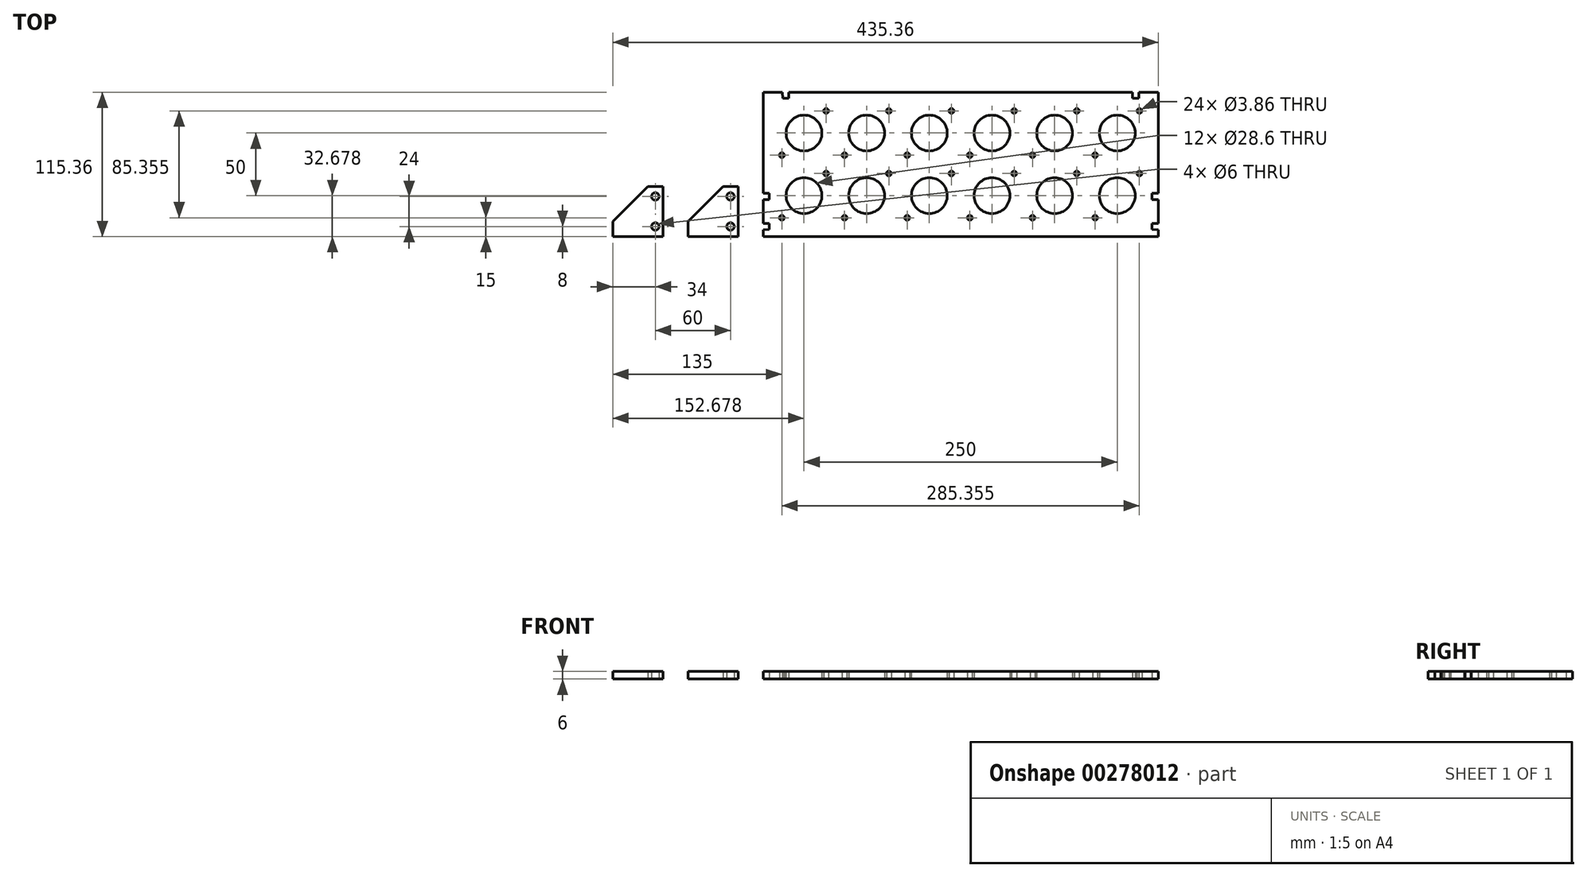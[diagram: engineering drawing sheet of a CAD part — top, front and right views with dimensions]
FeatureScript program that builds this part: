
annotation { "Feature Type Name" : "Feature", "Feature Type Description" : "" }
export const myFeature = defineFeature(function(context is Context, id is Id, definition is map)
    precondition{}
    {
        {
            assignVariable(context, id + "F0", {"name" : "X", "anyValue" : 6 * mm});
        }
        {
            var Q0;
            Q0=qCreatedBy(makeId("Top.planeOp"),FACE);
            var sketch = newSketch(context, id + "F1", { "sketchPlane" : qUnion([Q0])});
            skCircle(sketch, "E0", {"center": v(32.68, 32.68) * mm, "radius": 13.5 * mm, "construction": true});
            skCircle(sketch, "E1", {"center": v(15, 15) * mm, "radius": 1.93 * mm});
            skCircle(sketch, "E2", {"center": v(32.68, 32.68) * mm, "radius": 14.3 * mm});
            skCircle(sketch, "E3", {"center": v(50.36, 50.36) * mm, "radius": 1.93 * mm});
            skLineSegment(sketch, "E4", {"start": v(15, 15) * mm, "end": v(50.36, 50.36) * mm, "construction": true});
            skCircle(sketch, "E5.0.1.0", {"center": v(50.36, 100.36) * mm, "radius": 1.93 * mm});
            skCircle(sketch, "E5.0.1.1", {"center": v(32.68, 82.68) * mm, "radius": 14.3 * mm});
            skCircle(sketch, "E5.0.1.2", {"center": v(15, 65) * mm, "radius": 1.93 * mm});
            skCircle(sketch, "E5.1.0.0", {"center": v(100.36, 50.36) * mm, "radius": 1.93 * mm});
            skCircle(sketch, "E5.1.0.1", {"center": v(82.68, 32.68) * mm, "radius": 14.3 * mm});
            skCircle(sketch, "E5.1.0.2", {"center": v(65, 15) * mm, "radius": 1.93 * mm});
            skCircle(sketch, "E5.1.1.0", {"center": v(100.36, 100.36) * mm, "radius": 1.93 * mm});
            skCircle(sketch, "E5.1.1.1", {"center": v(82.68, 82.68) * mm, "radius": 14.3 * mm});
            skCircle(sketch, "E5.1.1.2", {"center": v(65, 65) * mm, "radius": 1.93 * mm});
            skCircle(sketch, "E5.2.0.0", {"center": v(150.36, 50.36) * mm, "radius": 1.93 * mm});
            skCircle(sketch, "E5.2.0.1", {"center": v(132.68, 32.68) * mm, "radius": 14.3 * mm});
            skCircle(sketch, "E5.2.0.2", {"center": v(115, 15) * mm, "radius": 1.93 * mm});
            skCircle(sketch, "E5.2.1.0", {"center": v(150.36, 100.36) * mm, "radius": 1.93 * mm});
            skCircle(sketch, "E5.2.1.1", {"center": v(132.68, 82.68) * mm, "radius": 14.3 * mm});
            skCircle(sketch, "E5.2.1.2", {"center": v(115, 65) * mm, "radius": 1.93 * mm});
            skCircle(sketch, "E5.3.0.0", {"center": v(200.36, 50.36) * mm, "radius": 1.93 * mm});
            skCircle(sketch, "E5.3.0.1", {"center": v(182.68, 32.68) * mm, "radius": 14.3 * mm});
            skCircle(sketch, "E5.3.0.2", {"center": v(165, 15) * mm, "radius": 1.93 * mm});
            skCircle(sketch, "E5.3.1.0", {"center": v(200.36, 100.36) * mm, "radius": 1.93 * mm});
            skCircle(sketch, "E5.3.1.1", {"center": v(182.68, 82.68) * mm, "radius": 14.3 * mm});
            skCircle(sketch, "E5.3.1.2", {"center": v(165, 65) * mm, "radius": 1.93 * mm});
            skLineSegment(sketch, "E5.direction1", {"start": v(15, 15) * mm, "end": v(65, 15) * mm, "construction": true});
            skLineSegment(sketch, "E5.direction2", {"start": v(15, 15) * mm, "end": v(15, 65) * mm, "construction": true});
            skCircle(sketch, "E6.0.4.0", {"center": v(250.36, 50.36) * mm, "radius": 1.93 * mm});
            skCircle(sketch, "E6.2.4.0", {"center": v(232.68, 32.68) * mm, "radius": 14.3 * mm});
            skCircle(sketch, "E6.4.4.0", {"center": v(215, 15) * mm, "radius": 1.93 * mm});
            skCircle(sketch, "E6.0.4.1", {"center": v(250.36, 100.36) * mm, "radius": 1.93 * mm});
            skCircle(sketch, "E6.2.4.1", {"center": v(232.68, 82.68) * mm, "radius": 14.3 * mm});
            skCircle(sketch, "E6.4.4.1", {"center": v(215, 65) * mm, "radius": 1.93 * mm});
            skCircle(sketch, "E6.0.5.0", {"center": v(300.36, 50.36) * mm, "radius": 1.93 * mm});
            skCircle(sketch, "E6.2.5.0", {"center": v(282.68, 32.68) * mm, "radius": 14.3 * mm});
            skCircle(sketch, "E6.4.5.0", {"center": v(265, 15) * mm, "radius": 1.93 * mm});
            skCircle(sketch, "E6.0.5.1", {"center": v(300.36, 100.36) * mm, "radius": 1.93 * mm});
            skCircle(sketch, "E6.2.5.1", {"center": v(282.68, 82.68) * mm, "radius": 14.3 * mm});
            skCircle(sketch, "E6.4.5.1", {"center": v(265, 65) * mm, "radius": 1.93 * mm});
            skLineSegment(sketch, "E7.bottom", {"start": v(0, 0) * mm, "end": v(315.36, 0) * mm});
            skLineSegment(sketch, "E7.top", {"start": v(0, 115.36) * mm, "end": v(15.4, 115.36) * mm});
            skLineSegment(sketch, "E8", {"start": v(300.36, 100.36) * mm, "end": v(300.36, 115.36) * mm, "construction": true});
            skLineSegment(sketch, "E9", {"start": v(300.36, 100.36) * mm, "end": v(315.36, 100.36) * mm, "construction": true});
            skLineSegment(sketch, "E10", {"start": v(15, 15) * mm, "end": v(0, 15) * mm, "construction": true});
            skLineSegment(sketch, "E11", {"start": v(15, 15) * mm, "end": v(15, 0) * mm, "construction": true});
            skLineSegment(sketch, "E12", {"start": v(-32, 40) * mm, "end": v(-60, 12) * mm});
            skLineSegment(sketch, "E13", {"start": v(-60, 12) * mm, "end": v(-60, 0) * mm});
            skLineSegment(sketch, "E14", {"start": v(-60, 0) * mm, "end": v(-20, 0) * mm});
            skLineSegment(sketch, "E15.trimOffspring", {"start": v(0, 0) * mm, "end": v(0, 5.4) * mm});
            skLineSegment(sketch, "E16.trimOffspring", {"start": v(315.36, 0) * mm, "end": v(315.36, 5.4) * mm});
            skLineSegment(sketch, "E17", {"start": v(-20, 0) * mm, "end": v(-20, 40) * mm});
            skLineSegment(sketch, "E18", {"start": v(-20, 40) * mm, "end": v(-23, 40) * mm});
            skLineSegment(sketch, "E19", {"start": v(-23, 40) * mm, "end": v(-23, 0) * mm, "construction": true});
            skLineSegment(sketch, "E20", {"start": v(-26, 0) * mm, "end": v(-26, 40) * mm, "construction": true});
            skLineSegment(sketch, "E21", {"start": v(-29, 40) * mm, "end": v(-29, 0) * mm, "construction": true});
            skLineSegment(sketch, "E22", {"start": v(-29, 40) * mm, "end": v(-32, 40) * mm});
            skLineSegment(sketch, "E23", {"start": v(-26, 40) * mm, "end": v(-29, 40) * mm});
            skLineSegment(sketch, "E24", {"start": v(-23, 40) * mm, "end": v(-26, 40) * mm});
            skCircle(sketch, "E25", {"center": v(-26, 32) * mm, "radius": 3 * mm});
            skCircle(sketch, "E26", {"center": v(-26, 8) * mm, "radius": 3 * mm});
            skLineSegment(sketch, "E27", {"start": v(0, 34.6) * mm, "end": v(5, 34.45) * mm});
            skLineSegment(sketch, "E28", {"start": v(5, 34.45) * mm, "end": v(5, 29.55) * mm});
            skLineSegment(sketch, "E29", {"start": v(5, 29.55) * mm, "end": v(0, 29.4) * mm});
            skLineSegment(sketch, "E30.trimOffspring", {"start": v(0, 34.6) * mm, "end": v(0, 115.36) * mm});
            skPoint(sketch, "E31", {"position": v(5, 32) * mm});
            skPoint(sketch, "E32", {"position": v(-26, 35) * mm});
            skPoint(sketch, "E33", {"position": v(-23, 32) * mm});
            skPoint(sketch, "E34", {"position": v(-26, 5) * mm});
            skLineSegment(sketch, "E35", {"start": v(0, 10.6) * mm, "end": v(5, 10.45) * mm});
            skLineSegment(sketch, "E36", {"start": v(5, 10.45) * mm, "end": v(5, 5.55) * mm});
            skLineSegment(sketch, "E37", {"start": v(5, 5.55) * mm, "end": v(0, 5.4) * mm});
            skLineSegment(sketch, "E38.trimOffspring", {"start": v(0, 10.6) * mm, "end": v(0, 29.4) * mm});
            skLineSegment(sketch, "E39", {"start": v(0, 34.6) * mm, "end": v(0, 29.4) * mm, "construction": true});
            skLineSegment(sketch, "E40", {"start": v(0, 5.4) * mm, "end": v(0, 10.6) * mm, "construction": true});
            skPoint(sketch, "E41", {"position": v(5, 8) * mm});
            skLineSegment(sketch, "E42", {"start": v(5, 10.45) * mm, "end": v(5, 10.85) * mm, "construction": true});
            skLineSegment(sketch, "E43", {"start": v(5, 10.85) * mm, "end": v(0, 11) * mm, "construction": true});
            skLineSegment(sketch, "E44", {"start": v(5, 5.55) * mm, "end": v(5, 5.15) * mm, "construction": true});
            skLineSegment(sketch, "E45", {"start": v(5, 5.15) * mm, "end": v(0, 5) * mm, "construction": true});
            skPoint(sketch, "E46", {"position": v(0, 8) * mm});
            skLineSegment(sketch, "E47", {"start": v(-23, 10.6) * mm, "end": v(-29, 10.6) * mm, "construction": true});
            skLineSegment(sketch, "E48", {"start": v(-23, 5.4) * mm, "end": v(-29, 5.4) * mm, "construction": true});
            skLineSegment(sketch, "E49.0.1.0", {"start": v(-83, 40) * mm, "end": v(-83, 0) * mm, "construction": true});
            skLineSegment(sketch, "E49.0.1.1", {"start": v(-120, 0) * mm, "end": v(-80, 0) * mm});
            skPoint(sketch, "E49.0.1.2", {"position": v(-86, 35) * mm});
            skPoint(sketch, "E49.0.1.3", {"position": v(-83, 32) * mm});
            skLineSegment(sketch, "E49.0.1.4", {"start": v(-80, 0) * mm, "end": v(-80, 40) * mm});
            skLineSegment(sketch, "E49.0.1.5", {"start": v(-120, 12) * mm, "end": v(-120, 0) * mm});
            skLineSegment(sketch, "E49.0.1.6", {"start": v(-86, 0) * mm, "end": v(-86, 40) * mm, "construction": true});
            skLineSegment(sketch, "E49.0.1.7", {"start": v(-92, 40) * mm, "end": v(-120, 12) * mm});
            skCircle(sketch, "E49.0.1.8", {"center": v(-86, 32) * mm, "radius": 3 * mm});
            skCircle(sketch, "E49.0.1.9", {"center": v(-86, 8) * mm, "radius": 3 * mm});
            skPoint(sketch, "E49.0.1.10", {"position": v(-86, 5) * mm});
            skLineSegment(sketch, "E49.0.1.11", {"start": v(-89, 40) * mm, "end": v(-89, 0) * mm, "construction": true});
            skLineSegment(sketch, "E49.0.1.12", {"start": v(-83, 5.4) * mm, "end": v(-89, 5.4) * mm, "construction": true});
            skLineSegment(sketch, "E49.0.1.13", {"start": v(-83, 10.6) * mm, "end": v(-89, 10.6) * mm, "construction": true});
            skLineSegment(sketch, "E49.0.1.14", {"start": v(-80, 40) * mm, "end": v(-83, 40) * mm});
            skLineSegment(sketch, "E49.0.1.15", {"start": v(-89, 40) * mm, "end": v(-92, 40) * mm});
            skLineSegment(sketch, "E49.0.1.16", {"start": v(-83, 40) * mm, "end": v(-86, 40) * mm});
            skLineSegment(sketch, "E49.0.1.17", {"start": v(-86, 40) * mm, "end": v(-89, 40) * mm});
            skLineSegment(sketch, "E49.direction1", {"start": v(-60, 0) * mm, "end": v(-35, 0) * mm, "construction": true});
            skLineSegment(sketch, "E49.direction2", {"start": v(-60, 0) * mm, "end": v(-120, 0) * mm, "construction": true});
            skLineSegment(sketch, "E50", {"start": v(157.68, 115.36) * mm, "end": v(157.68, 0) * mm, "construction": true});
            skLineSegment(sketch, "E51.MirrorCS", {"start": v(315.36, 34.6) * mm, "end": v(310.36, 34.45) * mm});
            skLineSegment(sketch, "E52.MirrorCS", {"start": v(310.36, 34.45) * mm, "end": v(310.36, 29.55) * mm});
            skLineSegment(sketch, "E53.MirrorCS", {"start": v(310.36, 29.55) * mm, "end": v(315.36, 29.4) * mm});
            skLineSegment(sketch, "E54.MirrorCS", {"start": v(315.36, 10.6) * mm, "end": v(310.36, 10.45) * mm});
            skLineSegment(sketch, "E55.MirrorCS", {"start": v(310.36, 5.55) * mm, "end": v(315.36, 5.4) * mm});
            skLineSegment(sketch, "E56.MirrorCS", {"start": v(310.36, 10.45) * mm, "end": v(310.36, 5.55) * mm});
            skLineSegment(sketch, "E57.trimOffspring", {"start": v(315.36, 34.6) * mm, "end": v(315.36, 115.36) * mm});
            skLineSegment(sketch, "E58.trimOffspring", {"start": v(315.36, 10.6) * mm, "end": v(315.36, 29.4) * mm});
            skLineSegment(sketch, "E59", {"start": v(264.63, 9.63) * mm, "end": v(287.91, 9.63) * mm, "construction": true});
            skLineSegment(sketch, "E60", {"start": v(287.91, 9.63) * mm, "end": v(305.73, 27.44) * mm, "construction": true});
            skLineSegment(sketch, "E61", {"start": v(305.73, 27.44) * mm, "end": v(305.73, 50.73) * mm, "construction": true});
            skLineSegment(sketch, "E62", {"start": v(300.73, 55.73) * mm, "end": v(277.44, 55.73) * mm, "construction": true});
            skLineSegment(sketch, "E63", {"start": v(277.44, 55.73) * mm, "end": v(259.63, 37.91) * mm, "construction": true});
            skLineSegment(sketch, "E64", {"start": v(259.63, 37.91) * mm, "end": v(259.63, 14.63) * mm, "construction": true});
            skPoint(sketch, "E65.visualSharp", {"position": v(305.73, 55.73) * mm});
            skArc(sketch, "E65.filletArc", {"start": v(305.73, 50.73) * mm, "mid": v(304.26, 54.26) * mm, "end": v(300.73, 55.73) * mm, "construction": true});
            skPoint(sketch, "E66.visualSharp", {"position": v(259.63, 9.63) * mm});
            skArc(sketch, "E66.filletArc", {"start": v(259.63, 14.63) * mm, "mid": v(261.1, 11.1) * mm, "end": v(264.63, 9.63) * mm, "construction": true});
            skLineSegment(sketch, "E67", {"start": v(259.63, 9.63) * mm, "end": v(265, 15) * mm, "construction": true});
            skLineSegment(sketch, "E68", {"start": v(300.36, 50.36) * mm, "end": v(305.73, 55.73) * mm, "construction": true});
            skLineSegment(sketch, "E69", {"start": v(265, 15) * mm, "end": v(300.36, 50.36) * mm, "construction": true});
            skPoint(sketch, "E70", {"position": v(261.1, 11.1) * mm});
            skPoint(sketch, "E71", {"position": v(304.26, 54.26) * mm});
            skLineSegment(sketch, "E72.0.1.0", {"start": v(305.73, 77.44) * mm, "end": v(305.73, 100.73) * mm, "construction": true});
            skArc(sketch, "E72.0.1.1", {"start": v(305.73, 100.73) * mm, "mid": v(304.26, 104.26) * mm, "end": v(300.73, 105.73) * mm, "construction": true});
            skLineSegment(sketch, "E72.0.1.2", {"start": v(300.73, 105.73) * mm, "end": v(277.44, 105.73) * mm, "construction": true});
            skLineSegment(sketch, "E72.0.1.3", {"start": v(277.44, 105.73) * mm, "end": v(259.63, 87.91) * mm, "construction": true});
            skLineSegment(sketch, "E72.0.1.4", {"start": v(259.63, 87.91) * mm, "end": v(259.63, 64.63) * mm, "construction": true});
            skArc(sketch, "E72.0.1.5", {"start": v(259.63, 64.63) * mm, "mid": v(261.1, 61.1) * mm, "end": v(264.63, 59.63) * mm, "construction": true});
            skLineSegment(sketch, "E72.0.1.6", {"start": v(264.63, 59.63) * mm, "end": v(287.91, 59.63) * mm, "construction": true});
            skLineSegment(sketch, "E72.0.1.7", {"start": v(287.91, 59.63) * mm, "end": v(305.73, 77.44) * mm, "construction": true});
            skLineSegment(sketch, "E72.1.0.0", {"start": v(255.73, 27.44) * mm, "end": v(255.73, 50.73) * mm, "construction": true});
            skArc(sketch, "E72.1.0.1", {"start": v(255.73, 50.73) * mm, "mid": v(254.26, 54.26) * mm, "end": v(250.73, 55.73) * mm, "construction": true});
            skLineSegment(sketch, "E72.1.0.2", {"start": v(250.73, 55.73) * mm, "end": v(227.44, 55.73) * mm, "construction": true});
            skLineSegment(sketch, "E72.1.0.3", {"start": v(227.44, 55.73) * mm, "end": v(209.63, 37.91) * mm, "construction": true});
            skLineSegment(sketch, "E72.1.0.4", {"start": v(209.63, 37.91) * mm, "end": v(209.63, 14.63) * mm, "construction": true});
            skArc(sketch, "E72.1.0.5", {"start": v(209.63, 14.63) * mm, "mid": v(211.1, 11.1) * mm, "end": v(214.63, 9.63) * mm, "construction": true});
            skLineSegment(sketch, "E72.1.0.6", {"start": v(214.63, 9.63) * mm, "end": v(237.91, 9.63) * mm, "construction": true});
            skLineSegment(sketch, "E72.1.0.7", {"start": v(237.91, 9.63) * mm, "end": v(255.73, 27.44) * mm, "construction": true});
            skLineSegment(sketch, "E72.1.1.0", {"start": v(255.73, 77.44) * mm, "end": v(255.73, 100.73) * mm, "construction": true});
            skArc(sketch, "E72.1.1.1", {"start": v(255.73, 100.73) * mm, "mid": v(254.26, 104.26) * mm, "end": v(250.73, 105.73) * mm, "construction": true});
            skLineSegment(sketch, "E72.1.1.2", {"start": v(250.73, 105.73) * mm, "end": v(227.44, 105.73) * mm, "construction": true});
            skLineSegment(sketch, "E72.1.1.3", {"start": v(227.44, 105.73) * mm, "end": v(209.63, 87.91) * mm, "construction": true});
            skLineSegment(sketch, "E72.1.1.4", {"start": v(209.63, 87.91) * mm, "end": v(209.63, 64.63) * mm, "construction": true});
            skArc(sketch, "E72.1.1.5", {"start": v(209.63, 64.63) * mm, "mid": v(211.1, 61.1) * mm, "end": v(214.63, 59.63) * mm, "construction": true});
            skLineSegment(sketch, "E72.1.1.6", {"start": v(214.63, 59.63) * mm, "end": v(237.91, 59.63) * mm, "construction": true});
            skLineSegment(sketch, "E72.1.1.7", {"start": v(237.91, 59.63) * mm, "end": v(255.73, 77.44) * mm, "construction": true});
            skLineSegment(sketch, "E72.direction1", {"start": v(264.63, 9.63) * mm, "end": v(214.63, 9.63) * mm, "construction": true});
            skLineSegment(sketch, "E72.direction2", {"start": v(264.63, 9.63) * mm, "end": v(264.63, 59.63) * mm, "construction": true});
            skLineSegment(sketch, "E73", {"start": v(15.4, 115.36) * mm, "end": v(15.55, 110.36) * mm});
            skLineSegment(sketch, "E74", {"start": v(15.55, 110.36) * mm, "end": v(20.45, 110.36) * mm});
            skLineSegment(sketch, "E75", {"start": v(20.45, 110.36) * mm, "end": v(20.6, 115.36) * mm});
            skLineSegment(sketch, "E76", {"start": v(294.76, 115.36) * mm, "end": v(294.9, 110.36) * mm});
            skLineSegment(sketch, "E77", {"start": v(294.9, 110.36) * mm, "end": v(299.8, 110.36) * mm});
            skLineSegment(sketch, "E78", {"start": v(299.8, 110.36) * mm, "end": v(299.95, 115.36) * mm});
            skLineSegment(sketch, "E79.trimOffspring", {"start": v(20.6, 115.36) * mm, "end": v(294.76, 115.36) * mm});
            skLineSegment(sketch, "E80.trimOffspring", {"start": v(299.95, 115.36) * mm, "end": v(315.36, 115.36) * mm});
            skLineSegment(sketch, "E81", {"start": v(15.4, 115.36) * mm, "end": v(20.6, 115.36) * mm, "construction": true});
            skLineSegment(sketch, "E82", {"start": v(294.76, 115.36) * mm, "end": v(299.95, 115.36) * mm, "construction": true});
            skPoint(sketch, "E83", {"position": v(18, 115.36) * mm});
            skPoint(sketch, "E84", {"position": v(18, 110.36) * mm});
            skPoint(sketch, "E85", {"position": v(297.36, 115.36) * mm});
            skPoint(sketch, "E86", {"position": v(297.36, 110.36) * mm});
            skLineSegment(sketch, "E87", {"start": v(18, 115.36) * mm, "end": v(18, 110.36) * mm, "construction": true});
            skLineSegment(sketch, "E88", {"start": v(0, 8) * mm, "end": v(5, 8) * mm, "construction": true});
            skSolve(sketch);
        }
        {
            var Q0;
            Q0 = qSketchRegion(id + "F1", true);
            extrude(context, id + "F2", {"entities" : qUnion([Q0]), "depth" : getVariable(context, 'X')});
        }
    });
